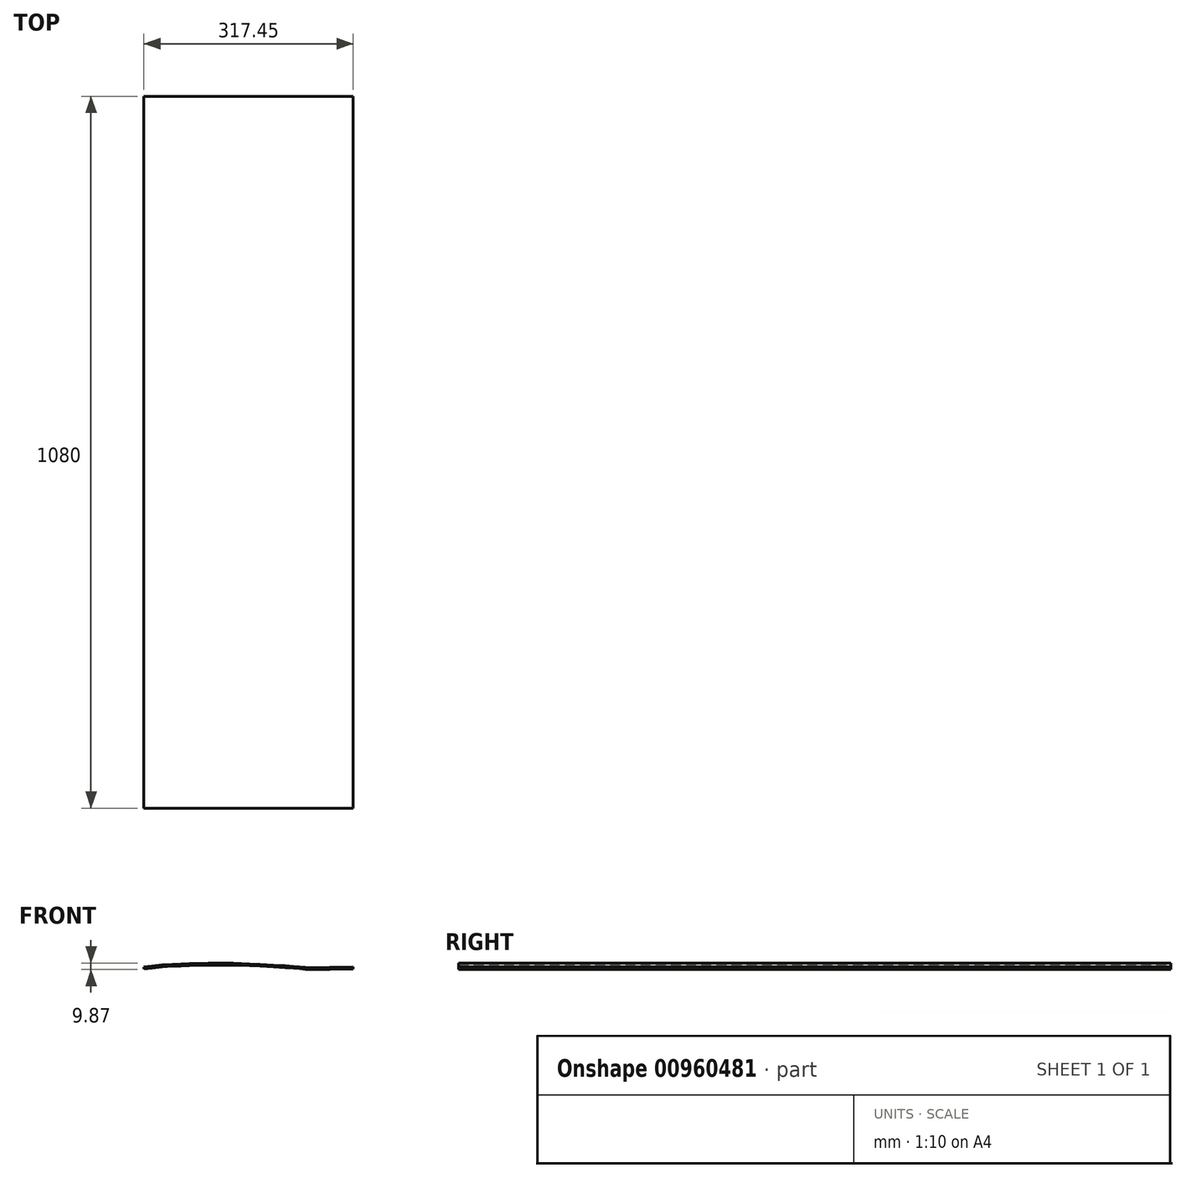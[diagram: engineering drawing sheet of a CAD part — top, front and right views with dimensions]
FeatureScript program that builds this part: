
annotation { "Feature Type Name" : "Feature", "Feature Type Description" : "" }
export const myFeature = defineFeature(function(context is Context, id is Id, definition is map)
    precondition{}
    {
        {
            var Q0;
            Q0=qCreatedBy(makeId("Front.planeOp"),FACE);
            var sketch = newSketch(context, id + "F0", { "sketchPlane" : qUnion([Q0])});
            skFitSpline(sketch, "E0", {"points": [v(1.46, 14.98) * mm, v(25.86, 17.96) * mm, v(60.73, 19.92) * mm, v(108.92, 20.99) * mm, v(150, 20.54) * mm, v(234.69, 15.69) * mm, v(255.3, 14.34) * mm, v(318.67, 15.14) * mm], "startDerivative": vector(219.23, 30.2) * mm, "endDerivative": vector(433.08, 9.63) * mm, "construction": true});
            skSolve(sketch);
        }
        {
            var Q0;
            Q0=qCreatedBy(makeId("Front.planeOp"),FACE);
            var sketch = newSketch(context, id + "F1", { "sketchPlane" : qUnion([Q0])});
            skFitSpline(sketch, "E1.0", {"points": [v(1.46, 14.98) * mm, v(9.35, 16.07) * mm, v(26.64, 18.45) * mm, v(60.8, 20.14) * mm, v(111.27, 21.12) * mm, v(146.95, 21.29) * mm, v(236.17, 15.92) * mm, v(254.35, 13.7) * mm, v(293.65, 14.58) * mm, v(318.67, 15.14) * mm], "construction": true});
            skFitSpline(sketch, "E2.0", {"points": [v(1.66, 13.5) * mm, v(3.95, 13.81) * mm, v(8.5, 14.44) * mm, v(15.45, 15.34) * mm, v(22.6, 16.16) * mm, v(30.06, 16.85) * mm, v(37.95, 17.4) * mm, v(44.94, 17.79) * mm, v(50.8, 18.05) * mm, v(55.36, 18.23) * mm, v(60.07, 18.4) * mm, v(64.95, 18.56) * mm, v(69.97, 18.7) * mm, v(76.78, 18.88) * mm, v(83.69, 19.04) * mm, v(90.52, 19.18) * mm, v(95.57, 19.28) * mm, v(100.5, 19.36) * mm, v(105.25, 19.44) * mm, v(109.8, 19.5) * mm, v(114.12, 19.55) * mm, v(118.3, 19.6) * mm, v(123.83, 19.61) * mm, v(129.43, 19.58) * mm, v(135.49, 19.48) * mm, v(140.35, 19.37) * mm, v(144.73, 19.23) * mm, v(148.5, 19.1) * mm, v(152.43, 18.95) * mm, v(157.7, 18.73) * mm, v(164.45, 18.42) * mm, v(171.52, 18.07) * mm, v(181.24, 17.56) * mm, v(193.65, 16.87) * mm, v(205.72, 16.15) * mm, v(214.74, 15.57) * mm, v(221.08, 15.16) * mm, v(225.92, 14.83) * mm, v(229.48, 14.57) * mm, v(231.97, 14.4) * mm, v(234.27, 14.22) * mm, v(236.37, 14.05) * mm, v(238.3, 13.9) * mm, v(240.66, 13.7) * mm, v(243.32, 13.48) * mm, v(246.23, 13.26) * mm, v(249.09, 13.07) * mm, v(252.1, 12.93) * mm, v(255.5, 12.82) * mm, v(259.46, 12.76) * mm, v(263.93, 12.74) * mm, v(268.86, 12.76) * mm, v(274.2, 12.8) * mm, v(281.79, 12.9) * mm, v(292.04, 13.07) * mm, v(305.17, 13.34) * mm, v(314.2, 13.54) * mm, v(318.7, 13.64) * mm]});
            skFitSpline(sketch, "E3.0", {"points": [v(1.25, 16.47) * mm, v(3.54, 16.78) * mm, v(8.1, 17.41) * mm, v(15.08, 18.32) * mm, v(22.29, 19.14) * mm, v(29.82, 19.84) * mm, v(37.77, 20.4) * mm, v(44.79, 20.78) * mm, v(50.68, 21.05) * mm, v(55.25, 21.23) * mm, v(59.97, 21.4) * mm, v(64.86, 21.56) * mm, v(69.89, 21.7) * mm, v(76.7, 21.88) * mm, v(83.62, 22.04) * mm, v(90.46, 22.18) * mm, v(95.51, 22.28) * mm, v(100.44, 22.36) * mm, v(105.2, 22.44) * mm, v(109.77, 22.5) * mm, v(114.1, 22.55) * mm, v(118.29, 22.6) * mm, v(123.83, 22.61) * mm, v(129.46, 22.58) * mm, v(135.55, 22.48) * mm, v(140.43, 22.37) * mm, v(144.83, 22.23) * mm, v(148.6, 22.1) * mm, v(152.56, 21.95) * mm, v(157.83, 21.73) * mm, v(164.6, 21.42) * mm, v(171.67, 21.07) * mm, v(181.4, 20.56) * mm, v(193.83, 19.87) * mm, v(205.9, 19.14) * mm, v(214.94, 18.57) * mm, v(221.28, 18.15) * mm, v(226.13, 17.82) * mm, v(229.7, 17.57) * mm, v(232.19, 17.38) * mm, v(234.5, 17.2) * mm, v(236.61, 17.04) * mm, v(238.54, 16.89) * mm, v(240.91, 16.7) * mm, v(243.56, 16.47) * mm, v(246.44, 16.25) * mm, v(249.26, 16.07) * mm, v(252.22, 15.93) * mm, v(255.57, 15.82) * mm, v(259.5, 15.76) * mm, v(263.93, 15.74) * mm, v(268.84, 15.76) * mm, v(274.16, 15.8) * mm, v(281.74, 15.9) * mm, v(291.98, 16.07) * mm, v(305.1, 16.34) * mm, v(314.13, 16.54) * mm, v(318.64, 16.64) * mm]});
            skLineSegment(sketch, "E4", {"start": v(1.25, 16.47) * mm, "end": v(1.66, 13.5) * mm});
            skLineSegment(sketch, "E5", {"start": v(318.64, 16.64) * mm, "end": v(318.7, 13.64) * mm});
            skSolve(sketch);
        }
        {
            var Q0;
            Q0=makeQuery(id+"F1.imprint","IMPRINT",FACE,{"disambiguationData":[TD([[makeQuery(id+"F1.imprint","IMPRINT",EDGE,{"derivedFrom":sQuery(id+"F1.wireOp",EDGE,"E2.0")}),1.0]])]});
            extrude(context, id + "F2", {"entities" : qUnion([Q0]), "depth" : (540 * 2) * mm, "offsetDistance" : 25 * mm});
        }
    });
